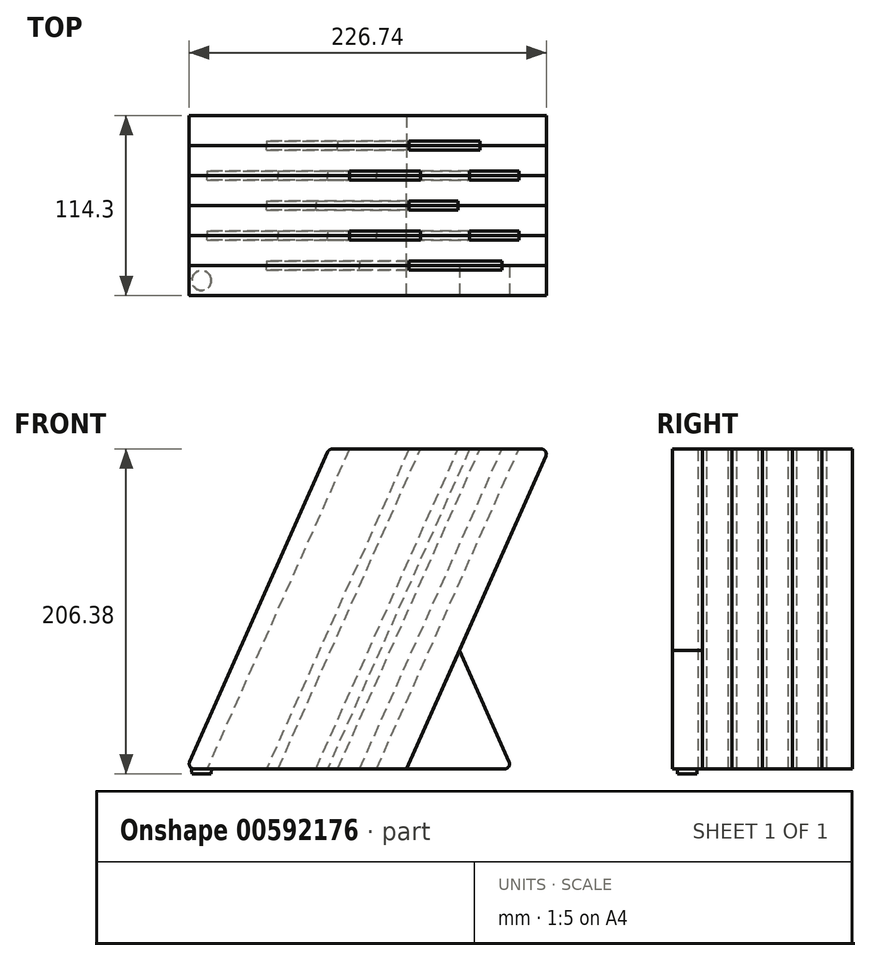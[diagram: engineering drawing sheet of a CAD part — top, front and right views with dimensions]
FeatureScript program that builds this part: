
annotation { "Feature Type Name" : "Feature", "Feature Type Description" : "" }
export const myFeature = defineFeature(function(context is Context, id is Id, definition is map)
    precondition{}
    {
        {
            var Q0;
            Q0=qCreatedBy(makeId("Front.planeOp"),FACE);
            var sketch = newSketch(context, id + "F0", { "sketchPlane" : qUnion([Q0])});
            skLineSegment(sketch, "E0", {"start": v(-73.99, 0) * mm, "end": v(16.48, 203.2) * mm});
            skLineSegment(sketch, "E1", {"start": v(16.48, 203.2) * mm, "end": v(-123.22, 203.2) * mm});
            skLineSegment(sketch, "E2", {"start": v(-123.22, 203.2) * mm, "end": v(-213.69, 0) * mm});
            skLineSegment(sketch, "E3", {"start": v(-213.69, 0) * mm, "end": v(-73.99, 0) * mm});
            skLineSegment(sketch, "E4", {"start": v(16.48, 203.2) * mm, "end": v(-81.34, 246.75) * mm, "construction": true});
            skPoint(sketch, "E5.orphan", {"position": v(-244.2, 0) * mm});
            skSolve(sketch);
        }
        {
            var Q0;
            Q0=makeQuery(id+"F0.imprint","IMPRINT",FACE,{"disambiguationData":[TD([[makeQuery(id+"F0.imprint","IMPRINT",EDGE,{"derivedFrom":sQuery(id+"F0.wireOp",EDGE,"E0")}),1.0]])]});
            extrude(context, id + "F1", {"entities" : qUnion([Q0]), "depth" : 19.05 * mm, "offsetDistance" : 25.4 * mm});
        }
        {
            var Q0;
            Q0=qCreatedBy(makeId("Front.planeOp"),FACE);
            cPlane(context, id + "F2", {"entities" : qUnion([Q0]), "cplaneType" : CPlaneType.OFFSET, "offset" : 19.05 * mm, "width" : 152.4 * mm, "height" : 152.4 * mm});
        }
        {
            var Q0;
            Q0=qCreatedBy(id+"F2.planeOp",FACE);
            cPlane(context, id + "F3", {"entities" : qUnion([Q0]), "cplaneType" : CPlaneType.OFFSET, "offset" : 19.05 * mm, "width" : 152.4 * mm, "height" : 152.4 * mm});
        }
        {
            var Q0;
            Q0=qCreatedBy(makeId("Front.planeOp"),FACE);
            cPlane(context, id + "F4", {"entities" : qUnion([Q0]), "cplaneType" : CPlaneType.OFFSET, "offset" : 19.05 * mm, "oppositeDirection" : true, "width" : 152.4 * mm, "height" : 152.4 * mm});
        }
        {
            var Q0;
            Q0=qCreatedBy(id+"F2.planeOp",FACE);
            var sketch = newSketch(context, id + "F5", { "sketchPlane" : qUnion([Q0])});
            skLineSegment(sketch, "E6.0", {"start": v(-213.69, 0) * mm, "end": v(-73.99, 0) * mm});
            skLineSegment(sketch, "E7.0", {"start": v(-223.52, 40.64) * mm, "end": v(-223.52, 0) * mm});
            skLineSegment(sketch, "E8.0", {"start": v(-123.22, 203.2) * mm, "end": v(-213.69, 0) * mm});
            skLineSegment(sketch, "E9.0", {"start": v(16.48, 203.2) * mm, "end": v(-123.22, 203.2) * mm});
            skLineSegment(sketch, "E10.0", {"start": v(-73.99, 0) * mm, "end": v(16.48, 203.2) * mm});
            skSolve(sketch);
        }
        {
            var Q0;
            Q0=makeQuery(id+"F5.imprint","IMPRINT",FACE,{"disambiguationData":[TD([[makeQuery(id+"F5.imprint","IMPRINT",EDGE,{"derivedFrom":sQuery(id+"F5.wireOp",EDGE,"E6.0")}),1.0]])]});
            extrude(context, id + "F6", {"entities" : qUnion([Q0]), "depth" : 19.05 * mm, "offsetDistance" : 25.4 * mm});
        }
        {
            var Q0;
            Q0=qCreatedBy(id+"F3.planeOp",FACE);
            var sketch = newSketch(context, id + "F7", { "sketchPlane" : qUnion([Q0])});
            skLineSegment(sketch, "E11.0", {"start": v(-123.22, 203.2) * mm, "end": v(-213.69, 0) * mm});
            skLineSegment(sketch, "E12.0", {"start": v(16.48, 203.2) * mm, "end": v(-123.22, 203.2) * mm});
            skLineSegment(sketch, "E13.0", {"start": v(-73.99, 0) * mm, "end": v(16.48, 203.2) * mm});
            skLineSegment(sketch, "E14.0", {"start": v(-213.69, 0) * mm, "end": v(-73.99, 0) * mm});
            skLineSegment(sketch, "E15.0", {"start": v(-223.52, 40.64) * mm, "end": v(-223.52, 0) * mm});
            skSolve(sketch);
        }
        {
            var Q0;
            Q0=makeQuery(id+"F7.imprint","IMPRINT",FACE,{"disambiguationData":[TD([[makeQuery(id+"F7.imprint","IMPRINT",EDGE,{"derivedFrom":sQuery(id+"F7.wireOp",EDGE,"E11.0")}),1.0]])]});
            extrude(context, id + "F8", {"entities" : qUnion([Q0]), "depth" : 19.05 * mm, "offsetDistance" : 25.4 * mm});
        }
        {
            var Q0;
            Q0=makeQuery(id+"F0.imprint","IMPRINT",FACE,{"disambiguationData":[TD([[makeQuery(id+"F0.imprint","IMPRINT",EDGE,{"derivedFrom":sQuery(id+"F0.wireOp",EDGE,"E0")}),1.0]])]});
            extrude(context, id + "F9", {"entities" : qUnion([Q0]), "oppositeDirection" : true, "depth" : 19.05 * mm, "offsetDistance" : 25.4 * mm});
        }
        {
            var Q0;
            Q0=qCreatedBy(id+"F4.planeOp",FACE);
            var sketch = newSketch(context, id + "F10", { "sketchPlane" : qUnion([Q0])});
            skLineSegment(sketch, "E16.0", {"start": v(-73.99, 0) * mm, "end": v(16.48, 203.2) * mm});
            skLineSegment(sketch, "E17.0", {"start": v(16.48, 203.2) * mm, "end": v(-123.22, 203.2) * mm});
            skLineSegment(sketch, "E18.0", {"start": v(-123.22, 203.2) * mm, "end": v(-213.69, 0) * mm});
            skLineSegment(sketch, "E19.0", {"start": v(-223.52, 40.64) * mm, "end": v(-223.52, 0) * mm});
            skLineSegment(sketch, "E20.0", {"start": v(-213.69, 0) * mm, "end": v(-73.99, 0) * mm});
            skSolve(sketch);
        }
        {
            var Q0;
            Q0=makeQuery(id+"F10.imprint","IMPRINT",FACE,{"disambiguationData":[TD([[makeQuery(id+"F10.imprint","IMPRINT",EDGE,{"derivedFrom":sQuery(id+"F10.wireOp",EDGE,"E16.0")}),1.0]])]});
            extrude(context, id + "F11", {"entities" : qUnion([Q0]), "oppositeDirection" : true, "depth" : 19.05 * mm, "offsetDistance" : 25.4 * mm});
        }
        {
            var Q0;
            Q0=qCreatedBy(id+"F3.planeOp",FACE);
            cPlane(context, id + "F12", {"entities" : qUnion([Q0]), "cplaneType" : CPlaneType.OFFSET, "offset" : 19.05 * mm, "width" : 152.4 * mm, "height" : 152.4 * mm});
        }
        {
            var Q0;
            Q0=qCreatedBy(id+"F12.planeOp",FACE);
            var sketch = newSketch(context, id + "F13", { "sketchPlane" : qUnion([Q0])});
            skLineSegment(sketch, "E21.0", {"start": v(-213.69, 0) * mm, "end": v(-73.99, 0) * mm});
            skLineSegment(sketch, "E22.0", {"start": v(-223.52, 40.64) * mm, "end": v(-223.52, 0) * mm});
            skLineSegment(sketch, "E23.0", {"start": v(-123.22, 203.2) * mm, "end": v(-213.69, 0) * mm});
            skLineSegment(sketch, "E24.0", {"start": v(16.48, 203.2) * mm, "end": v(-123.22, 203.2) * mm});
            skLineSegment(sketch, "E25.0", {"start": v(-73.99, 0) * mm, "end": v(16.48, 203.2) * mm});
            skSolve(sketch);
        }
        {
            var Q0;
            Q0=makeQuery(id+"F13.imprint","IMPRINT",FACE,{"disambiguationData":[TD([[makeQuery(id+"F13.imprint","IMPRINT",EDGE,{"derivedFrom":sQuery(id+"F13.wireOp",EDGE,"E21.0")}),1.0]])]});
            extrude(context, id + "F14", {"entities" : qUnion([Q0]), "depth" : 19.05 * mm, "offsetDistance" : 25.4 * mm});
        }
        {
            var Q0;
            Q0=makeQuery(id+"F11.opExtrude","CAP_FACE",FACE,{"disambiguationData":[OSD([sQuery(id+"F10.wireOp",EDGE,"E16.0"),sQuery(id+"F10.wireOp",EDGE,"E17.0"),sQuery(id+"F10.wireOp",EDGE,"E18.0"),sQuery(id+"F10.wireOp",EDGE,"E19.0"),sQuery(id+"F10.wireOp",EDGE,"E20.0")])],"isStart":true});
            var sketch = newSketch(context, id + "F15", { "sketchPlane" : qUnion([Q0])});
            skLineSegment(sketch, "E26", {"start": v(-72.42, 203.2) * mm, "end": v(-162.89, 0) * mm});
            skLineSegment(sketch, "E27", {"start": v(-162.89, 0) * mm, "end": v(-117.7, 0) * mm});
            skLineSegment(sketch, "E28", {"start": v(-117.7, 0) * mm, "end": v(-27.23, 203.2) * mm});
            skLineSegment(sketch, "E29", {"start": v(-27.23, 203.2) * mm, "end": v(-72.42, 203.2) * mm});
            skSolve(sketch);
        }
        {
            var Q0;
            Q0=makeQuery(id+"F15.imprint","IMPRINT",FACE,{"disambiguationData":[TD([[makeQuery(id+"F15.imprint","IMPRINT",EDGE,{"derivedFrom":sQuery(id+"F15.wireOp",EDGE,"E26")}),1.0]])]});
            extrude(context, id + "F16", {"entities" : qUnion([Q0]), "operationType" : NewBodyOperationType.REMOVE, "oppositeDirection" : true, "depth" : 2.8 * mm, "offsetDistance" : 25.4 * mm});
        }
        {
            var Q0;
            Q0=makeQuery(id+"F15.imprint","IMPRINT",FACE,{"disambiguationData":[TD([[makeQuery(id+"F15.imprint","IMPRINT",EDGE,{"derivedFrom":sQuery(id+"F15.wireOp",EDGE,"E26")}),1.0]])]});
            extrude(context, id + "F17", {"entities" : qUnion([Q0]), "operationType" : NewBodyOperationType.REMOVE, "depth" : 2.8 * mm, "offsetDistance" : 25.4 * mm});
        }
        {
            var Q0;
            Q0=makeQuery(id+"F9.opExtrude","CAP_FACE",FACE,{"disambiguationData":[OSD([sQuery(id+"F0.wireOp",EDGE,"E0"),sQuery(id+"F0.wireOp",EDGE,"E1"),sQuery(id+"F0.wireOp",EDGE,"E2"),sQuery(id+"F0.wireOp",EDGE,"NX70fIWh-2Hpz-98Tc-NKQz-7SD6WKST9EiD"),sQuery(id+"F0.wireOp",EDGE,"E3")])],"isStart":true});
            var sketch = newSketch(context, id + "F18", { "sketchPlane" : qUnion([Q0])});
            skLineSegment(sketch, "E30", {"start": v(-110.3, 203.2) * mm, "end": v(-200.78, 0) * mm});
            skLineSegment(sketch, "E31", {"start": v(-200.78, 0) * mm, "end": v(-155.6, 0) * mm});
            skLineSegment(sketch, "E32", {"start": v(-155.6, 0) * mm, "end": v(-65.12, 203.2) * mm});
            skLineSegment(sketch, "E33", {"start": v(-65.12, 203.2) * mm, "end": v(-110.3, 203.2) * mm});
            skLineSegment(sketch, "E34", {"start": v(-33.85, 203.2) * mm, "end": v(-124.32, 0) * mm});
            skLineSegment(sketch, "E35", {"start": v(-124.32, 0) * mm, "end": v(-93.04, 0) * mm});
            skLineSegment(sketch, "E36", {"start": v(-93.04, 0) * mm, "end": v(-2.57, 203.2) * mm});
            skLineSegment(sketch, "E37", {"start": v(-2.57, 203.2) * mm, "end": v(-33.85, 203.2) * mm});
            skSolve(sketch);
        }
        {
            var Q0;
            Q0=makeQuery(id+"F18.imprint","IMPRINT",FACE,{"disambiguationData":[TD([[makeQuery(id+"F18.imprint","IMPRINT",EDGE,{"derivedFrom":sQuery(id+"F18.wireOp",EDGE,"E30")}),1.0]])]});
            var Q1;
            Q1=makeQuery(id+"F18.imprint","IMPRINT",FACE,{"disambiguationData":[TD([[makeQuery(id+"F18.imprint","IMPRINT",EDGE,{"derivedFrom":sQuery(id+"F18.wireOp",EDGE,"E34")}),1.0]])]});
            extrude(context, id + "F19", {"entities" : qUnion([Q0, Q1]), "operationType" : NewBodyOperationType.REMOVE, "oppositeDirection" : true, "depth" : 2.8 * mm, "offsetDistance" : 25.4 * mm});
        }
        {
            var Q0;
            Q0=makeQuery(id+"F18.imprint","IMPRINT",FACE,{"disambiguationData":[TD([[makeQuery(id+"F18.imprint","IMPRINT",EDGE,{"derivedFrom":sQuery(id+"F18.wireOp",EDGE,"E34")}),1.0]])]});
            var Q1;
            Q1=makeQuery(id+"F18.imprint","IMPRINT",FACE,{"disambiguationData":[TD([[makeQuery(id+"F18.imprint","IMPRINT",EDGE,{"derivedFrom":sQuery(id+"F18.wireOp",EDGE,"E30")}),1.0]])]});
            extrude(context, id + "F20", {"entities" : qUnion([Q0, Q1]), "operationType" : NewBodyOperationType.REMOVE, "depth" : 2.8 * mm, "offsetDistance" : 25.4 * mm});
        }
        {
            var Q0;
            Q0=makeQuery(id+"F1.opExtrude","CAP_FACE",FACE,{"disambiguationData":[OSD([sQuery(id+"F0.wireOp",EDGE,"E0"),sQuery(id+"F0.wireOp",EDGE,"E1"),sQuery(id+"F0.wireOp",EDGE,"E2"),sQuery(id+"F0.wireOp",EDGE,"NX70fIWh-2Hpz-98Tc-NKQz-7SD6WKST9EiD"),sQuery(id+"F0.wireOp",EDGE,"E3")])],"isStart":false});
            var sketch = newSketch(context, id + "F21", { "sketchPlane" : qUnion([Q0])});
            skLineSegment(sketch, "E38", {"start": v(-72.42, 203.2) * mm, "end": v(-162.89, 0) * mm});
            skLineSegment(sketch, "E39", {"start": v(-162.89, 0) * mm, "end": v(-131.6, 0) * mm});
            skLineSegment(sketch, "E40", {"start": v(-131.6, 0) * mm, "end": v(-41.14, 203.2) * mm});
            skLineSegment(sketch, "E41", {"start": v(-41.14, 203.2) * mm, "end": v(-72.42, 203.2) * mm});
            skSolve(sketch);
        }
        {
            var Q0;
            Q0=makeQuery(id+"F21.imprint","IMPRINT",FACE,{"disambiguationData":[TD([[makeQuery(id+"F21.imprint","IMPRINT",EDGE,{"derivedFrom":sQuery(id+"F21.wireOp",EDGE,"E38")}),1.0]])]});
            extrude(context, id + "F22", {"entities" : qUnion([Q0]), "operationType" : NewBodyOperationType.REMOVE, "oppositeDirection" : true, "depth" : 2.8 * mm, "offsetDistance" : 25.4 * mm});
        }
        {
            var Q0;
            Q0=makeQuery(id+"F21.imprint","IMPRINT",FACE,{"disambiguationData":[TD([[makeQuery(id+"F21.imprint","IMPRINT",EDGE,{"derivedFrom":sQuery(id+"F21.wireOp",EDGE,"E38")}),1.0]])]});
            extrude(context, id + "F23", {"entities" : qUnion([Q0]), "operationType" : NewBodyOperationType.REMOVE, "depth" : 2.8 * mm, "offsetDistance" : 25.4 * mm});
        }
        {
            var Q0;
            Q0=makeQuery(id+"F6.opExtrude","CAP_FACE",FACE,{"disambiguationData":[OSD([sQuery(id+"F5.wireOp",EDGE,"E6.0"),sQuery(id+"F5.wireOp",EDGE,"E7.0"),sQuery(id+"F5.wireOp",EDGE,"E8.0"),sQuery(id+"F5.wireOp",EDGE,"E9.0"),sQuery(id+"F5.wireOp",EDGE,"E10.0")])],"isStart":false});
            var sketch = newSketch(context, id + "F24", { "sketchPlane" : qUnion([Q0])});
            skLineSegment(sketch, "E42.0", {"start": v(-110.3, 203.2) * mm, "end": v(-200.78, 0) * mm});
            skLineSegment(sketch, "E43.0", {"start": v(-65.12, 203.2) * mm, "end": v(-110.3, 203.2) * mm});
            skLineSegment(sketch, "E44.0", {"start": v(-155.6, 0) * mm, "end": v(-65.12, 203.2) * mm});
            skLineSegment(sketch, "E45.0", {"start": v(-200.78, 0) * mm, "end": v(-155.6, 0) * mm});
            skLineSegment(sketch, "E46.0", {"start": v(-33.85, 203.2) * mm, "end": v(-124.32, 0) * mm});
            skLineSegment(sketch, "E47.0", {"start": v(-2.57, 203.2) * mm, "end": v(-33.85, 203.2) * mm});
            skLineSegment(sketch, "E48.0", {"start": v(-93.04, 0) * mm, "end": v(-2.57, 203.2) * mm});
            skLineSegment(sketch, "E49.0", {"start": v(-124.32, 0) * mm, "end": v(-93.04, 0) * mm});
            skSolve(sketch);
        }
        {
            var Q0;
            Q0=makeQuery(id+"F24.imprint","IMPRINT",FACE,{"disambiguationData":[TD([[makeQuery(id+"F24.imprint","IMPRINT",EDGE,{"derivedFrom":sQuery(id+"F24.wireOp",EDGE,"E42.0")}),1.0]])]});
            var Q1;
            Q1=makeQuery(id+"F24.imprint","IMPRINT",FACE,{"disambiguationData":[TD([[makeQuery(id+"F24.imprint","IMPRINT",EDGE,{"derivedFrom":sQuery(id+"F24.wireOp",EDGE,"E46.0")}),1.0]])]});
            extrude(context, id + "F25", {"entities" : qUnion([Q0, Q1]), "operationType" : NewBodyOperationType.REMOVE, "oppositeDirection" : true, "depth" : 2.8 * mm, "offsetDistance" : 25.4 * mm});
        }
        {
            var Q0;
            Q0=makeQuery(id+"F24.imprint","IMPRINT",FACE,{"disambiguationData":[TD([[makeQuery(id+"F24.imprint","IMPRINT",EDGE,{"derivedFrom":sQuery(id+"F24.wireOp",EDGE,"E46.0")}),1.0]])]});
            var Q1;
            Q1=makeQuery(id+"F24.imprint","IMPRINT",FACE,{"disambiguationData":[TD([[makeQuery(id+"F24.imprint","IMPRINT",EDGE,{"derivedFrom":sQuery(id+"F24.wireOp",EDGE,"E42.0")}),1.0]])]});
            extrude(context, id + "F26", {"entities" : qUnion([Q0, Q1]), "operationType" : NewBodyOperationType.REMOVE, "depth" : 2.8 * mm, "offsetDistance" : 25.4 * mm});
        }
        {
            var Q0;
            Q0=makeQuery(id+"F8.opExtrude","CAP_FACE",FACE,{"disambiguationData":[OSD([sQuery(id+"F7.wireOp",EDGE,"E11.0"),sQuery(id+"F7.wireOp",EDGE,"E12.0"),sQuery(id+"F7.wireOp",EDGE,"E13.0"),sQuery(id+"F7.wireOp",EDGE,"E14.0"),sQuery(id+"F7.wireOp",EDGE,"E15.0")])],"isStart":false});
            var sketch = newSketch(context, id + "F27", { "sketchPlane" : qUnion([Q0])});
            skLineSegment(sketch, "E50", {"start": v(-72.42, 203.2) * mm, "end": v(-162.89, 0) * mm});
            skLineSegment(sketch, "E51", {"start": v(-162.89, 0) * mm, "end": v(-103.8, 0) * mm});
            skLineSegment(sketch, "E52", {"start": v(-103.8, 0) * mm, "end": v(-13.33, 203.2) * mm});
            skLineSegment(sketch, "E53", {"start": v(-13.33, 203.2) * mm, "end": v(-72.42, 203.2) * mm});
            skSolve(sketch);
        }
        {
            var Q0;
            Q0=makeQuery(id+"F27.imprint","IMPRINT",FACE,{"disambiguationData":[TD([[makeQuery(id+"F27.imprint","IMPRINT",EDGE,{"derivedFrom":sQuery(id+"F27.wireOp",EDGE,"E50")}),1.0]])]});
            extrude(context, id + "F28", {"entities" : qUnion([Q0]), "operationType" : NewBodyOperationType.REMOVE, "oppositeDirection" : true, "depth" : 2.8 * mm, "offsetDistance" : 25.4 * mm});
        }
        {
            var Q0;
            Q0=makeQuery(id+"F27.imprint","IMPRINT",FACE,{"disambiguationData":[TD([[makeQuery(id+"F27.imprint","IMPRINT",EDGE,{"derivedFrom":sQuery(id+"F27.wireOp",EDGE,"E50")}),1.0]])]});
            extrude(context, id + "F29", {"entities" : qUnion([Q0]), "operationType" : NewBodyOperationType.REMOVE, "depth" : 2.8 * mm, "offsetDistance" : 25.4 * mm});
        }
        {
            var Q0;
            Q0=makeQuery(id+"F14.opExtrude","CAP_FACE",FACE,{"disambiguationData":[OSD([sQuery(id+"F13.wireOp",EDGE,"E21.0"),sQuery(id+"F13.wireOp",EDGE,"E22.0"),sQuery(id+"F13.wireOp",EDGE,"E23.0"),sQuery(id+"F13.wireOp",EDGE,"E24.0"),sQuery(id+"F13.wireOp",EDGE,"E25.0")])],"isStart":false});
            var sketch = newSketch(context, id + "F30", { "sketchPlane" : qUnion([Q0])});
            skLineSegment(sketch, "E54", {"start": v(-73.99, 0) * mm, "end": v(-40.41, 75.41) * mm});
            skLineSegment(sketch, "E55", {"start": v(-40.41, 75.41) * mm, "end": v(-6.83, 0) * mm});
            skLineSegment(sketch, "E56", {"start": v(-6.83, 0) * mm, "end": v(-73.99, 0) * mm});
            skSolve(sketch);
        }
        {
            var Q0;
            Q0=makeQuery(id+"F30.imprint","IMPRINT",FACE,{"disambiguationData":[TD([[makeQuery(id+"F30.imprint","IMPRINT",EDGE,{"derivedFrom":sQuery(id+"F30.wireOp",EDGE,"E54")}),-1.0]])]});
            extrude(context, id + "F31", {"entities" : qUnion([Q0]), "oppositeDirection" : true, "depth" : 19.05 * mm, "offsetDistance" : 25.4 * mm});
        }
        {
            var Q0;
            Q0=makeQuery(id+"F11.opExtrude","SWEPT_EDGE",EDGE,{"disambiguationData":[OSD([sQuery(id+"F10.wireOp",EDGE,"E16.0"),sQuery(id+"F10.wireOp",EDGE,"E17.0")])]});
            var Q1;
            Q1=makeQuery(id+"F9.opExtrude","SWEPT_EDGE",EDGE,{"disambiguationData":[OSD([sQuery(id+"F0.wireOp",EDGE,"E0"),sQuery(id+"F0.wireOp",EDGE,"E1")])]});
            var Q2;
            Q2=makeQuery(id+"F1.opExtrude","SWEPT_EDGE",EDGE,{"disambiguationData":[OSD([sQuery(id+"F0.wireOp",EDGE,"E0"),sQuery(id+"F0.wireOp",EDGE,"E1")])]});
            var Q3;
            Q3=makeQuery(id+"F6.opExtrude","SWEPT_EDGE",EDGE,{"disambiguationData":[OSD([sQuery(id+"F5.wireOp",EDGE,"E9.0"),sQuery(id+"F5.wireOp",EDGE,"E10.0")])]});
            var Q4;
            Q4=makeQuery(id+"F8.opExtrude","SWEPT_EDGE",EDGE,{"disambiguationData":[OSD([sQuery(id+"F7.wireOp",EDGE,"E12.0"),sQuery(id+"F7.wireOp",EDGE,"E13.0")])]});
            var Q5;
            Q5=makeQuery(id+"F14.opExtrude","SWEPT_EDGE",EDGE,{"disambiguationData":[OSD([sQuery(id+"F13.wireOp",EDGE,"E24.0"),sQuery(id+"F13.wireOp",EDGE,"E25.0")])]});
            fillet(context, id + "F32", {"entities" : qUnion([Q0, Q1, Q2, Q3, Q4, Q5]), "radius" : 3.17 * mm, "tangentPropagation" : true, "allowEdgeOverflow" : false});
        }
        {
            var Q0;
            Q0=makeQuery(id+"F11.opExtrude","SWEPT_EDGE",EDGE,{"disambiguationData":[OSD([sQuery(id+"F10.wireOp",EDGE,"E17.0"),sQuery(id+"F10.wireOp",EDGE,"E18.0")])]});
            var Q1;
            Q1=makeQuery(id+"F9.opExtrude","SWEPT_EDGE",EDGE,{"disambiguationData":[OSD([sQuery(id+"F0.wireOp",EDGE,"E1"),sQuery(id+"F0.wireOp",EDGE,"E2")])]});
            var Q2;
            Q2=makeQuery(id+"F1.opExtrude","SWEPT_EDGE",EDGE,{"disambiguationData":[OSD([sQuery(id+"F0.wireOp",EDGE,"E1"),sQuery(id+"F0.wireOp",EDGE,"E2")])]});
            var Q3;
            Q3=makeQuery(id+"F6.opExtrude","SWEPT_EDGE",EDGE,{"disambiguationData":[OSD([sQuery(id+"F5.wireOp",EDGE,"E8.0"),sQuery(id+"F5.wireOp",EDGE,"E9.0")])]});
            var Q4;
            Q4=makeQuery(id+"F8.opExtrude","SWEPT_EDGE",EDGE,{"disambiguationData":[OSD([sQuery(id+"F7.wireOp",EDGE,"E11.0"),sQuery(id+"F7.wireOp",EDGE,"E12.0")])]});
            var Q5;
            Q5=makeQuery(id+"F14.opExtrude","SWEPT_EDGE",EDGE,{"disambiguationData":[OSD([sQuery(id+"F13.wireOp",EDGE,"E23.0"),sQuery(id+"F13.wireOp",EDGE,"E24.0")])]});
            fillet(context, id + "F33", {"entities" : qUnion([Q0, Q1, Q2, Q3, Q4, Q5]), "radius" : 3.17 * mm, "tangentPropagation" : true, "allowEdgeOverflow" : false});
        }
        {
            var Q0;
            Q0=makeQuery(id+"F14.opExtrude","SWEPT_FACE",FACE,{"disambiguationData":[OSD([sQuery(id+"F13.wireOp",EDGE,"E21.0")])]});
            var sketch = newSketch(context, id + "F34", { "sketchPlane" : qUnion([Q0])});
            skCircle(sketch, "E57", {"center": v(-204.16, 66.68) * mm, "radius": 6.35 * mm});
            skPoint(sketch, "E57.centerSnap0", {"position": v(-213.69, 66.68) * mm});
            skSolve(sketch);
        }
        {
            var Q0;
            Q0=makeQuery(id+"F34.imprint","IMPRINT",FACE,{"disambiguationData":[TD([[makeQuery(id+"F34.imprint","IMPRINT",EDGE,{"derivedFrom":sQuery(id+"F34.wireOp",EDGE,"E57")}),1.0]])]});
            extrude(context, id + "F35", {"entities" : qUnion([Q0]), "depth" : 3.17 * mm, "offsetDistance" : 25.4 * mm, "hasDraft" : true, "draftAngle" : 5 * degree, "draftPullDirection" : true});
        }
        {
            var Q0;
            Q0=makeQuery(id+"F31.opExtrude","SWEPT_EDGE",EDGE,{"disambiguationData":[OSD([sQuery(id+"F30.wireOp",EDGE,"E55"),sQuery(id+"F30.wireOp",EDGE,"E56")])]});
            fillet(context, id + "F36", {"entities" : qUnion([Q0]), "radius" : 3.17 * mm, "tangentPropagation" : true, "allowEdgeOverflow" : false});
        }
        {
            var Q0;
            Q0=makeQuery(id+"F11.opExtrude","SWEPT_EDGE",EDGE,{"disambiguationData":[OSD([sQuery(id+"F10.wireOp",EDGE,"E18.0"),sQuery(id+"F10.wireOp",EDGE,"E20.0")])]});
            var Q1;
            Q1=makeQuery(id+"F9.opExtrude","SWEPT_EDGE",EDGE,{"disambiguationData":[OSD([sQuery(id+"F0.wireOp",EDGE,"E2"),sQuery(id+"F0.wireOp",EDGE,"E3")])]});
            var Q2;
            Q2=makeQuery(id+"F1.opExtrude","SWEPT_EDGE",EDGE,{"disambiguationData":[OSD([sQuery(id+"F0.wireOp",EDGE,"E2"),sQuery(id+"F0.wireOp",EDGE,"E3")])]});
            var Q3;
            Q3=makeQuery(id+"F6.opExtrude","SWEPT_EDGE",EDGE,{"disambiguationData":[OSD([sQuery(id+"F5.wireOp",EDGE,"E6.0"),sQuery(id+"F5.wireOp",EDGE,"E8.0")])]});
            var Q4;
            Q4=makeQuery(id+"F8.opExtrude","SWEPT_EDGE",EDGE,{"disambiguationData":[OSD([sQuery(id+"F7.wireOp",EDGE,"E11.0"),sQuery(id+"F7.wireOp",EDGE,"E14.0")])]});
            var Q5;
            Q5=makeQuery(id+"F14.opExtrude","SWEPT_EDGE",EDGE,{"disambiguationData":[OSD([sQuery(id+"F13.wireOp",EDGE,"E21.0"),sQuery(id+"F13.wireOp",EDGE,"E23.0")])]});
            fillet(context, id + "F37", {"entities" : qUnion([Q0, Q1, Q2, Q3, Q4, Q5]), "radius" : 3.17 * mm, "tangentPropagation" : true, "allowEdgeOverflow" : false});
        }
    });
